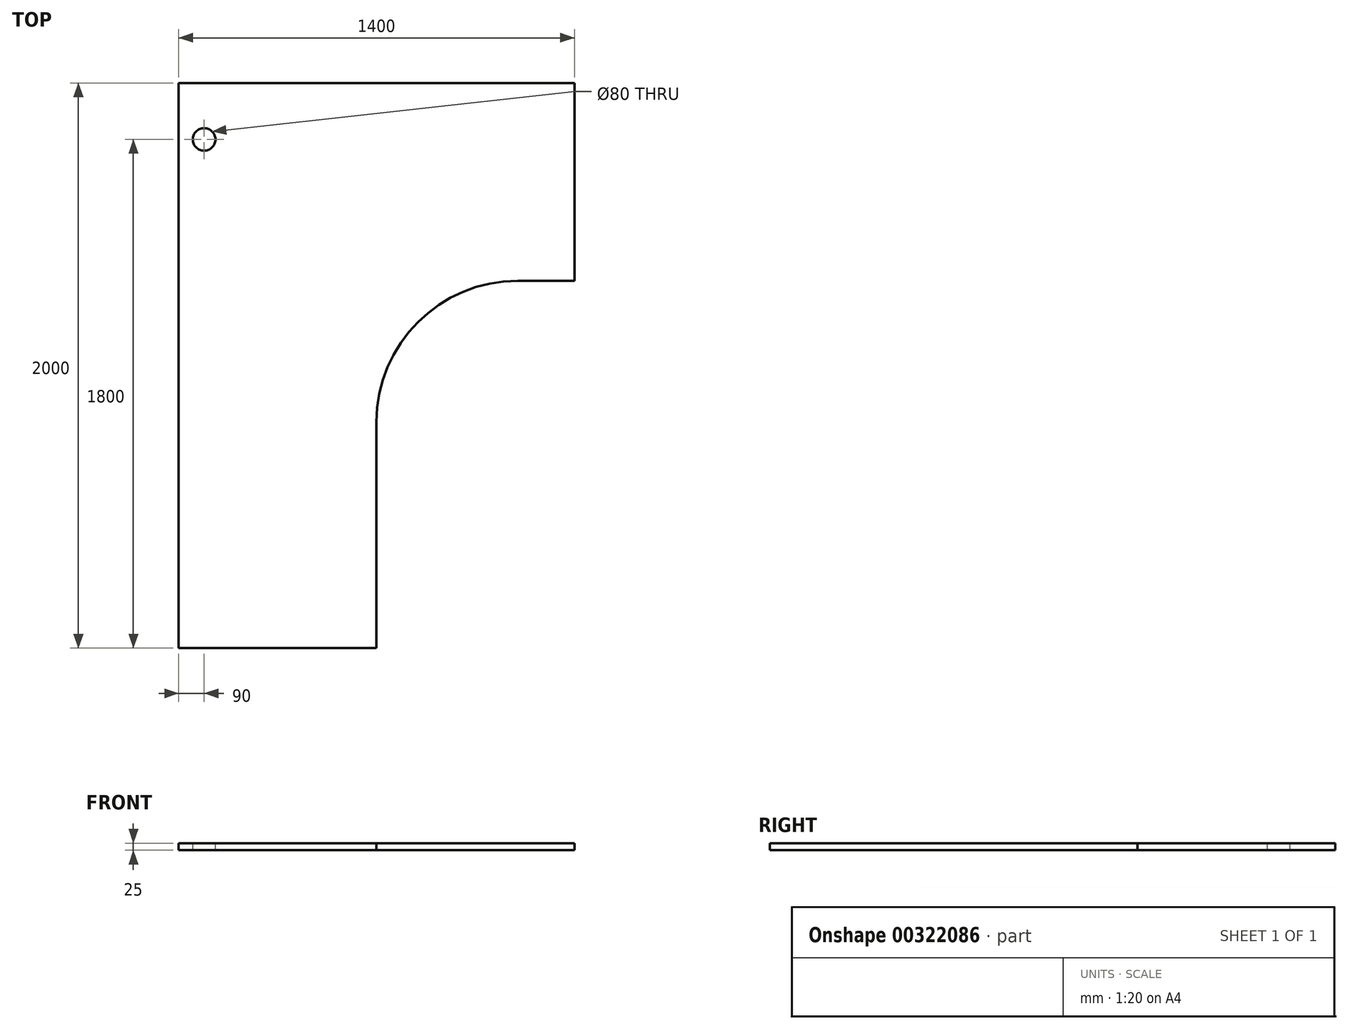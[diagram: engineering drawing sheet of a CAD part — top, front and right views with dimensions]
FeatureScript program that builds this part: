
annotation { "Feature Type Name" : "Feature", "Feature Type Description" : "" }
export const myFeature = defineFeature(function(context is Context, id is Id, definition is map)
    precondition{}
    {
        {
            var Q0;
            Q0=qCreatedBy(makeId("Top.planeOp"),FACE);
            var sketch = newSketch(context, id + "F0", { "sketchPlane" : qUnion([Q0])});
            skLineSegment(sketch, "E0", {"start": v(0, 0) * mm, "end": v(1400, 0) * mm});
            skLineSegment(sketch, "E1", {"start": v(1400, 0) * mm, "end": v(1400, -700) * mm});
            skLineSegment(sketch, "E2", {"start": v(1400, -700) * mm, "end": v(1200, -700) * mm});
            skLineSegment(sketch, "E3", {"start": v(0, 0) * mm, "end": v(0, -2000) * mm});
            skLineSegment(sketch, "E4", {"start": v(0, -2000) * mm, "end": v(700, -2000) * mm});
            skLineSegment(sketch, "E5", {"start": v(700, -2000) * mm, "end": v(700, -1200) * mm});
            skArc(sketch, "E6", {"start": v(1200, -700) * mm, "mid": v(846.45, -846.45) * mm, "end": v(700, -1200) * mm});
            skSolve(sketch);
        }
        {
            var Q0;
            Q0=makeQuery(id+"F0.imprint","IMPRINT",FACE,{"disambiguationData":[TD([[makeQuery(id+"F0.imprint","IMPRINT",EDGE,{"derivedFrom":sQuery(id+"F0.wireOp",EDGE,"E0")}),-1.0]])]});
            extrude(context, id + "F1", {"entities" : qUnion([Q0]), "depth" : 25 * mm});
        }
        {
            var Q0;
            Q0=makeQuery(id+"F1.opExtrude","CAP_FACE",FACE,{"disambiguationData":[OSD([sQuery(id+"F0.wireOp",EDGE,"E0"),sQuery(id+"F0.wireOp",EDGE,"E1"),sQuery(id+"F0.wireOp",EDGE,"E2"),sQuery(id+"F0.wireOp",EDGE,"E3"),sQuery(id+"F0.wireOp",EDGE,"E4"),sQuery(id+"F0.wireOp",EDGE,"E5"),sQuery(id+"F0.wireOp",EDGE,"E6")])],"isStart":false});
            var sketch = newSketch(context, id + "F2", { "sketchPlane" : qUnion([Q0])});
            skCircle(sketch, "E7", {"center": v(90, -200) * mm, "radius": 40 * mm});
            skSolve(sketch);
        }
        {
            var Q0;
            Q0=makeQuery(id+"F2.imprint","IMPRINT",FACE,{"disambiguationData":[TD([[makeQuery(id+"F2.imprint","IMPRINT",EDGE,{"derivedFrom":sQuery(id+"F2.wireOp",EDGE,"E7")}),1.0]])]});
            extrude(context, id + "F3", {"entities" : qUnion([Q0]), "operationType" : NewBodyOperationType.REMOVE, "endBound" : BoundingType.UP_TO_NEXT, "oppositeDirection" : true, "depth" : 25 * mm});
        }
    });
